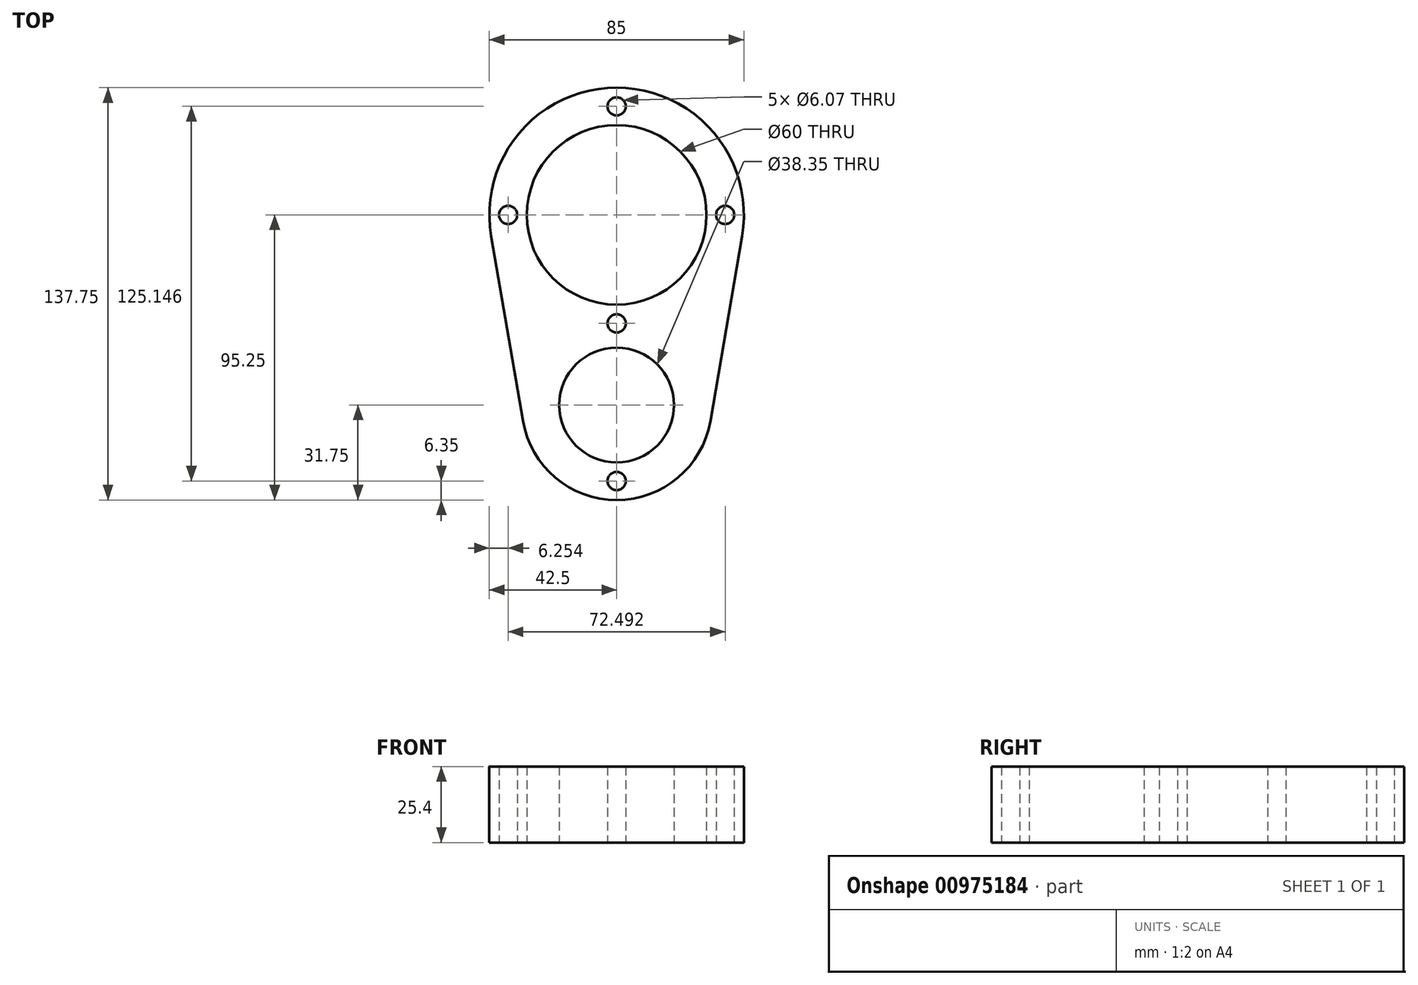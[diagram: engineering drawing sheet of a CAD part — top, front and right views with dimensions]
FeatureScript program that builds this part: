
annotation { "Feature Type Name" : "Feature", "Feature Type Description" : "" }
export const myFeature = defineFeature(function(context is Context, id is Id, definition is map)
    precondition{}
    {
        {
            var Q0;
            Q0=qCreatedBy(makeId("Top.planeOp"),FACE);
            var sketch = newSketch(context, id + "F0", { "sketchPlane" : qUnion([Q0])});
            skCircle(sketch, "E0", {"center": v(0, 0) * mm, "radius": 30 * mm});
            skCircle(sketch, "E1", {"center": v(0, -63.5) * mm, "radius": 19.18 * mm});
            skLineSegment(sketch, "E2", {"start": v(-41.89, -7.2) * mm, "end": v(-41.89, -7.2) * mm});
            skLineSegment(sketch, "E3", {"start": v(31.3, -68.88) * mm, "end": v(41.89, -7.2) * mm});
            skLineSegment(sketch, "E4", {"start": v(-41.89, -7.2) * mm, "end": v(-31.3, -68.88) * mm});
            skArc(sketch, "E5", {"start": v(41.89, -7.2) * mm, "mid": v(0, 42.5) * mm, "end": v(-41.89, -7.2) * mm});
            skArc(sketch, "E6", {"start": v(-41.89, -7.2) * mm, "mid": v(0, -42.5) * mm, "end": v(41.89, -7.2) * mm, "construction": true});
            skArc(sketch, "E7", {"start": v(31.3, -68.88) * mm, "mid": v(0, -31.75) * mm, "end": v(-31.3, -68.87) * mm, "construction": true});
            skArc(sketch, "E8", {"start": v(-31.3, -68.88) * mm, "mid": v(0, -95.25) * mm, "end": v(31.3, -68.88) * mm});
            skCircle(sketch, "E9", {"center": v(0, 0) * mm, "radius": 36.25 * mm, "construction": true});
            skCircle(sketch, "E10", {"center": v(0, 36.25) * mm, "radius": 3.04 * mm});
            skCircle(sketch, "E11", {"center": v(0, -88.9) * mm, "radius": 3.04 * mm});
            skCircle(sketch, "E12.1.0", {"center": v(-36.25, 0) * mm, "radius": 3.04 * mm});
            skCircle(sketch, "E12.2.0", {"center": v(0, -36.25) * mm, "radius": 3.04 * mm});
            skCircle(sketch, "E12.3.0", {"center": v(36.25, 0) * mm, "radius": 3.04 * mm});
            skSolve(sketch);
        }
        {
            var Q0;
            Q0 = qSketchRegion(id + "F0", true);
            extrude(context, id + "F1", {"entities" : qUnion([Q0]), "depth" : 25.4 * mm, "offsetDistance" : 25.4 * mm});
        }
    });
